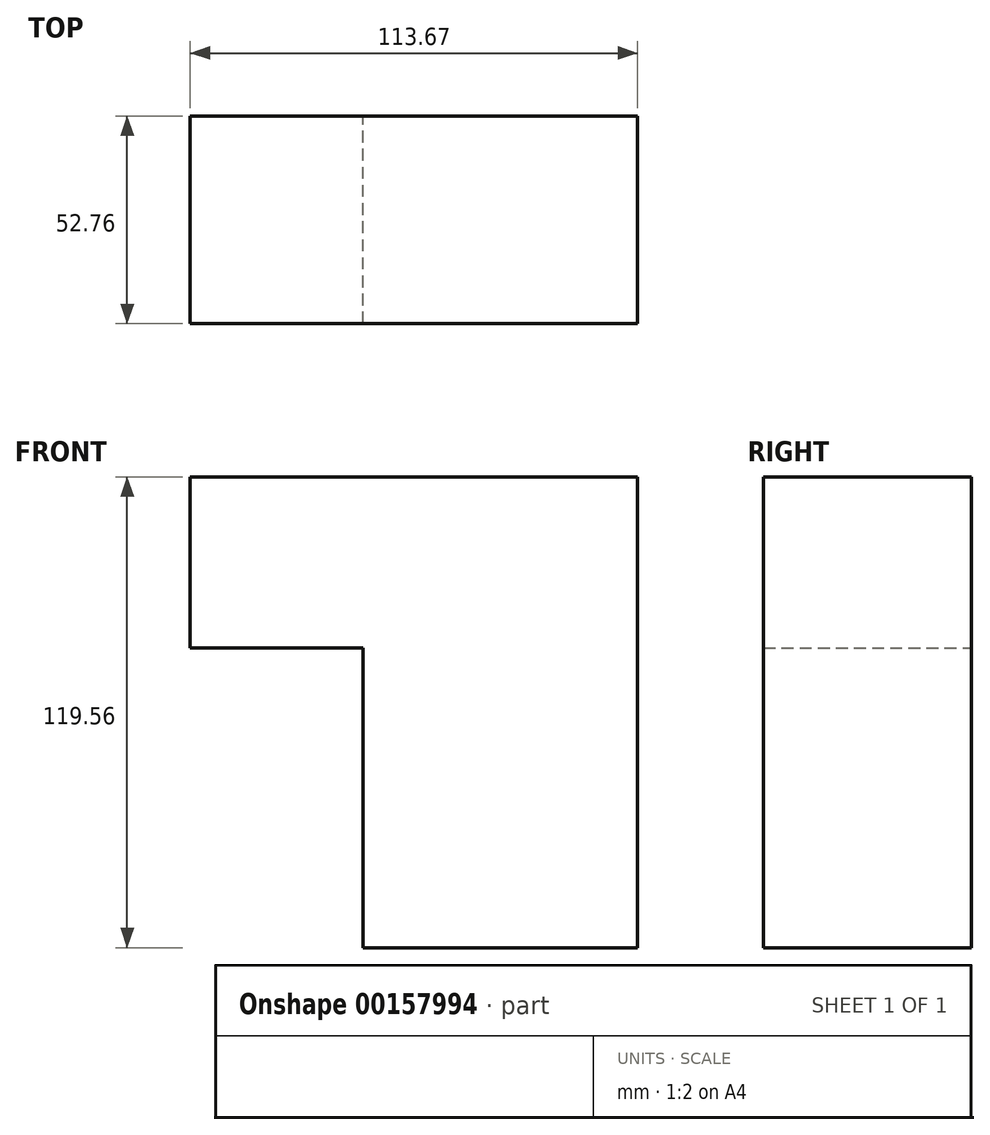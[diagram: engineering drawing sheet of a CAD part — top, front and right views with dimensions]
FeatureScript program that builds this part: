
annotation { "Feature Type Name" : "Feature", "Feature Type Description" : "" }
export const myFeature = defineFeature(function(context is Context, id is Id, definition is map)
    precondition{}
    {
        {
            var Q0;
            Q0=qCreatedBy(makeId("Right.planeOp"),FACE);
            var sketch = newSketch(context, id + "F0", { "sketchPlane" : qUnion([Q0])});
            skLineSegment(sketch, "E0.bottom", {"start": v(0, 0) * mm, "end": v(-52.76, 0) * mm});
            skLineSegment(sketch, "E0.top", {"start": v(0, 43.36) * mm, "end": v(-52.76, 43.36) * mm});
            skLineSegment(sketch, "E0.left", {"start": v(0, 0) * mm, "end": v(0, 43.36) * mm});
            skLineSegment(sketch, "E0.right", {"start": v(-52.76, 0) * mm, "end": v(-52.76, 43.36) * mm});
            skSolve(sketch);
        }
        {
            var Q0;
            Q0=makeQuery(id+"F0.imprint","IMPRINT",FACE,{"disambiguationData":[TD([[makeQuery(id+"F0.imprint","IMPRINT",EDGE,{"derivedFrom":sQuery(id+"F0.wireOp",EDGE,"E0.bottom")}),-1.0]])]});
            extrude(context, id + "F1", {"entities" : qUnion([Q0]), "depth" : 113.66 * mm});
        }
        {
            var Q0;
            Q0=makeQuery(id+"F1.opExtrude","SWEPT_FACE",FACE,{"disambiguationData":[OSD([sQuery(id+"F0.wireOp",EDGE,"E0.bottom")])]});
            var sketch = newSketch(context, id + "F2", { "sketchPlane" : qUnion([Q0])});
            skLineSegment(sketch, "E1.bottom", {"start": v(43.94, 52.76) * mm, "end": v(113.67, 52.76) * mm});
            skLineSegment(sketch, "E1.top", {"start": v(43.94, 0) * mm, "end": v(113.67, 0) * mm});
            skLineSegment(sketch, "E1.left", {"start": v(43.94, 52.76) * mm, "end": v(43.94, 0) * mm});
            skLineSegment(sketch, "E1.right", {"start": v(113.67, 52.76) * mm, "end": v(113.67, 0) * mm});
            skSolve(sketch);
        }
        {
            var Q0;
            Q0=makeQuery(id+"F2.imprint","IMPRINT",FACE,{"disambiguationData":[TD([[makeQuery(id+"F2.imprint","IMPRINT",EDGE,{"derivedFrom":sQuery(id+"F2.wireOp",EDGE,"E1.bottom")}),1.0]])]});
            extrude(context, id + "F3", {"entities" : qUnion([Q0]), "operationType" : NewBodyOperationType.ADD, "depth" : 76.2 * mm});
        }
    });
